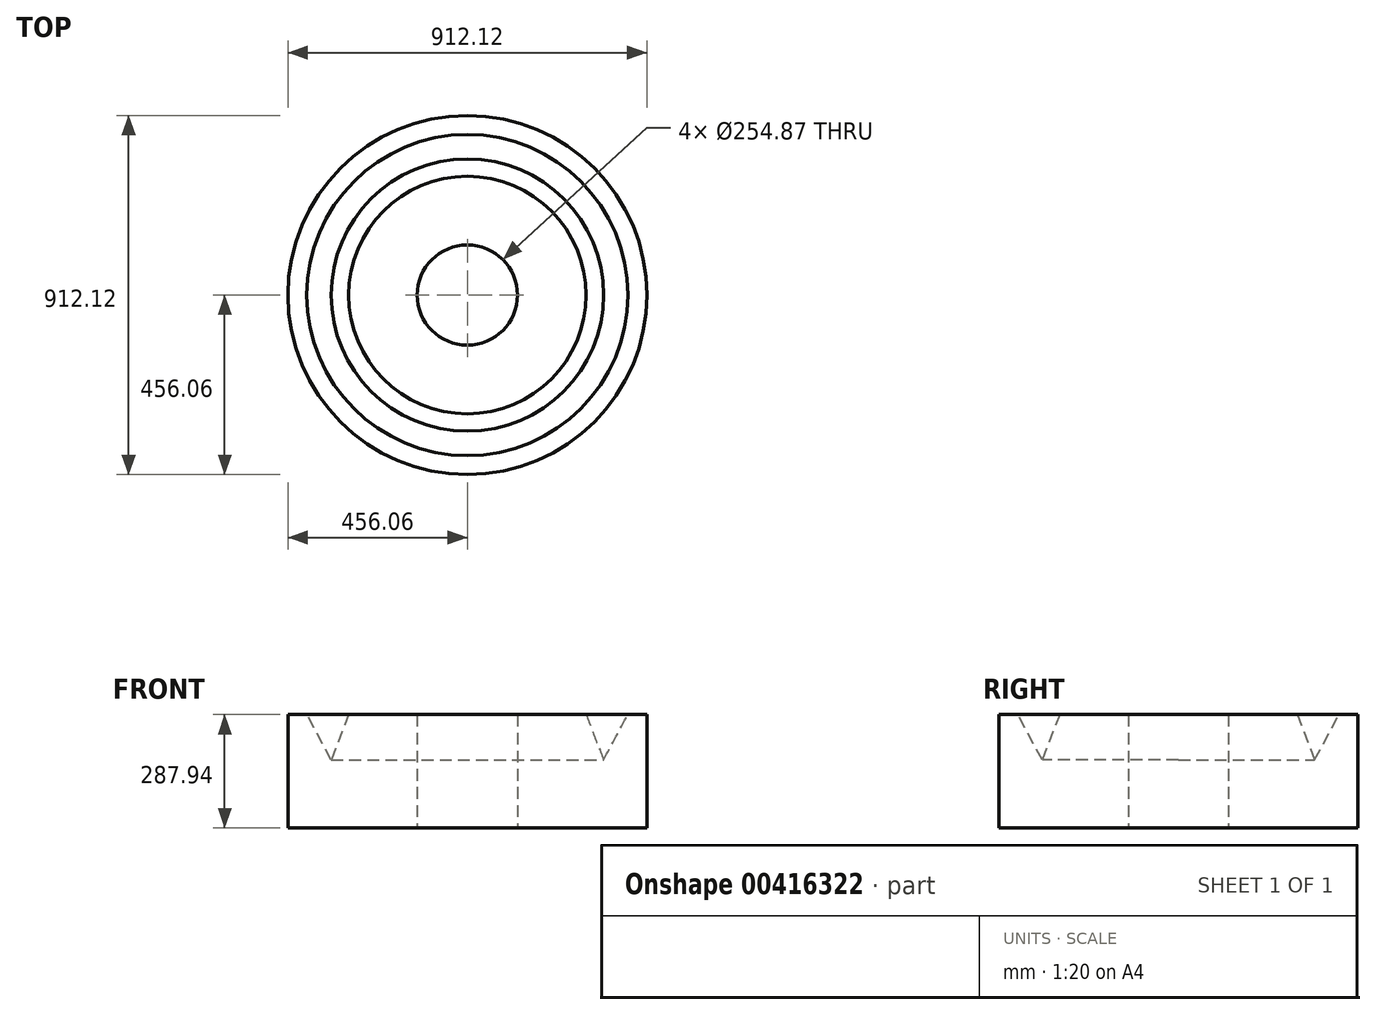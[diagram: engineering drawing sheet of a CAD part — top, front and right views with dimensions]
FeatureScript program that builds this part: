
annotation { "Feature Type Name" : "Feature", "Feature Type Description" : "" }
export const myFeature = defineFeature(function(context is Context, id is Id, definition is map)
    precondition{}
    {
        {
            var Q0;
            Q0=qCreatedBy(makeId("Front.planeOp"),FACE);
            var sketch = newSketch(context, id + "F0", { "sketchPlane" : qUnion([Q0])});
            skLineSegment(sketch, "E0.bottom", {"start": v(456.06, -172.72) * mm, "end": v(127.44, -172.72) * mm});
            skLineSegment(sketch, "E0.top", {"start": v(456.06, 115.22) * mm, "end": v(127.44, 115.22) * mm});
            skLineSegment(sketch, "E0.left", {"start": v(456.06, -172.72) * mm, "end": v(456.06, 115.22) * mm});
            skLineSegment(sketch, "E0.right", {"start": v(127.44, -172.72) * mm, "end": v(127.44, 115.22) * mm});
            skPoint(sketch, "E0.middle", {"position": v(291.75, -28.75) * mm});
            skLineSegment(sketch, "E1", {"start": v(-354.55, -235.32) * mm, "end": v(204.12, -588.98) * mm, "construction": true});
            skLineSegment(sketch, "E2", {"start": v(625.07, -614.02) * mm, "end": v(1008.47, -174.29) * mm, "construction": true});
            skLineSegment(sketch, "E3", {"start": v(0, 0) * mm, "end": v(0, 196.59) * mm, "construction": true});
            skSolve(sketch);
        }
        {
            var Q0;
            Q0=makeQuery(id+"F0.imprint","IMPRINT",FACE,{"disambiguationData":[TD([[makeQuery(id+"F0.imprint","IMPRINT",EDGE,{"derivedFrom":sQuery(id+"F0.wireOp",EDGE,"E0.bottom")}),-1.0]])]});
            var Q1;
            Q1=sQuery(id+"F0.wireOp",EDGE,"E3");
            revolve(context, id + "F1", {"entities" : qUnion([Q0]), "axis" : qUnion([Q1]), "revolveType" : RevolveType.FULL});
        }
        {
            var Q0;
            Q0=qCreatedBy(makeId("Front.planeOp"),FACE);
            var sketch = newSketch(context, id + "F2", { "sketchPlane" : qUnion([Q0])});
            skLineSegment(sketch, "E4", {"start": v(-471.14, 233.08) * mm, "end": v(-346.02, 0) * mm});
            skLineSegment(sketch, "E5", {"start": v(-346.02, 0) * mm, "end": v(-256.4, 233.08) * mm});
            skLineSegment(sketch, "E6", {"start": v(-471.14, 233.08) * mm, "end": v(-256.4, 233.08) * mm});
            skSolve(sketch);
        }
        {
            var Q0;
            Q0 = qSketchRegion(id + "F2", true);
            var Q1;
            Q1=sQuery(id+"F0.wireOp",EDGE,"E3");
            revolve(context, id + "F3", {"operationType" : NewBodyOperationType.REMOVE, "entities" : qUnion([Q0]), "axis" : qUnion([Q1]), "revolveType" : RevolveType.FULL});
        }
    });
